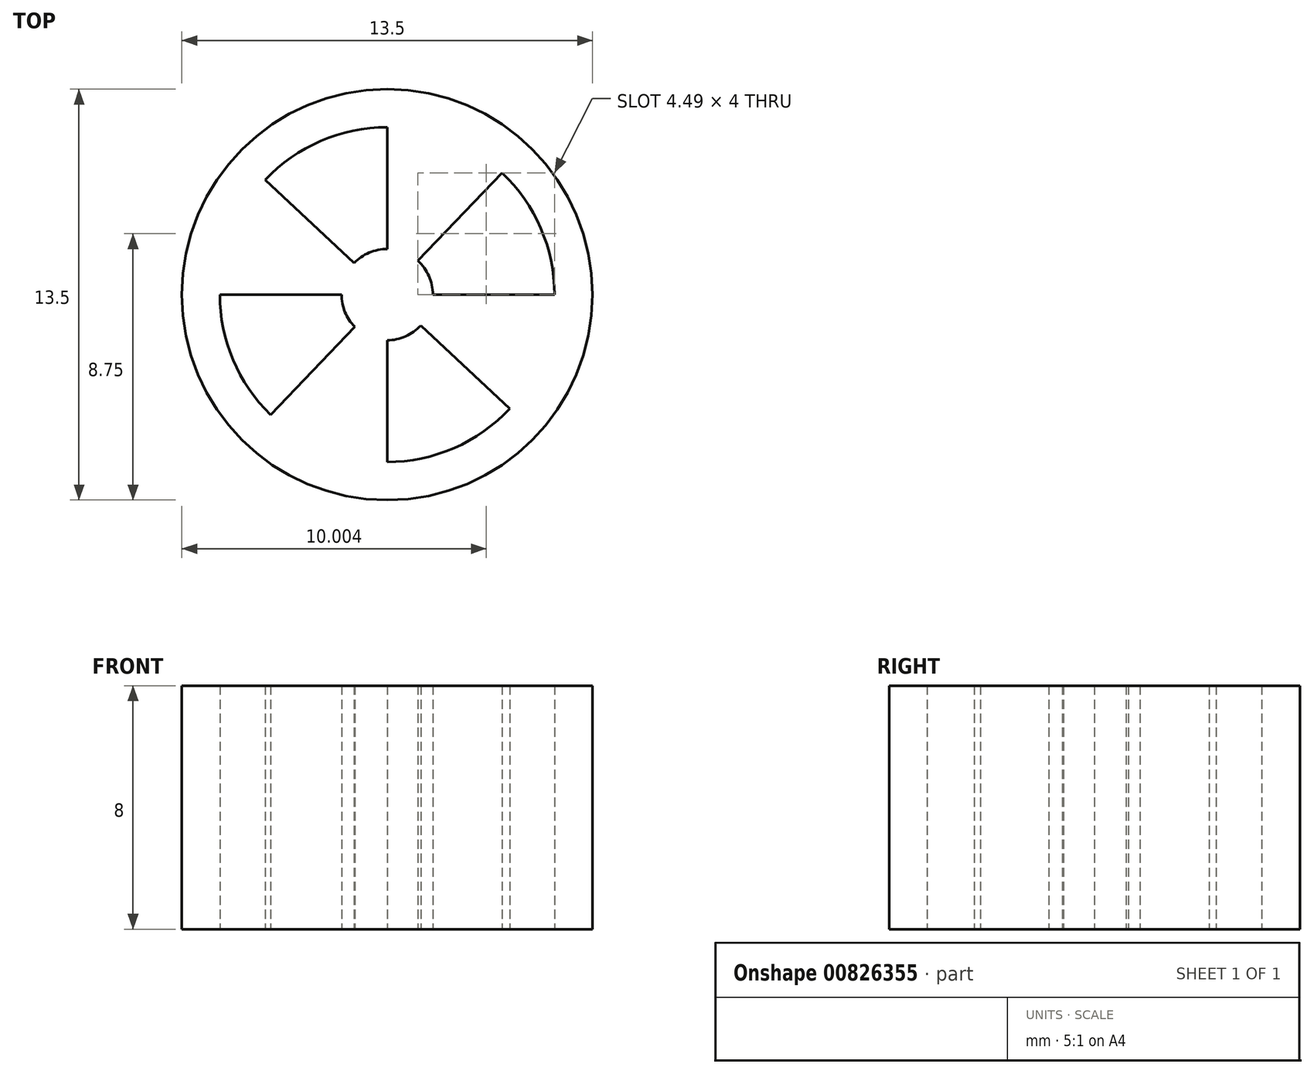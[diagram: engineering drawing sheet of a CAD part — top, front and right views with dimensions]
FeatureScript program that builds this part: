
annotation { "Feature Type Name" : "Feature", "Feature Type Description" : "" }
export const myFeature = defineFeature(function(context is Context, id is Id, definition is map)
    precondition{}
    {
        {
            var Q0;
            Q0=qCreatedBy(makeId("Top.planeOp"),FACE);
            var sketch = newSketch(context, id + "F0", { "sketchPlane" : qUnion([Q0])});
            skCircle(sketch, "E0", {"center": v(0, 0) * mm, "radius": 6.75 * mm});
            skSolve(sketch);
        }
        {
            var Q0;
            Q0=makeQuery(id+"F0.imprint","IMPRINT",FACE,{"disambiguationData":[TD([[makeQuery(id+"F0.imprint","IMPRINT",EDGE,{"derivedFrom":sQuery(id+"F0.wireOp",EDGE,"E0")}),1.0]])]});
            extrude(context, id + "F1", {"entities" : qUnion([Q0]), "depth" : 8 * mm, "offsetDistance" : 25 * mm});
        }
        {
            var Q0;
            Q0=makeQuery(id+"F1.opExtrude","CAP_FACE",FACE,{"disambiguationData":[OSD([sQuery(id+"F0.wireOp",EDGE,"E0")])],"isStart":true});
            var sketch = newSketch(context, id + "F2", { "sketchPlane" : qUnion([Q0])});
            skCircle(sketch, "E1", {"center": v(0, 0) * mm, "radius": 5.5 * mm});
            skCircle(sketch, "E2", {"center": v(0, 0) * mm, "radius": 1.5 * mm});
            skLineSegment(sketch, "E3", {"start": v(0, 0) * mm, "end": v(0, 5.5) * mm});
            skLineSegment(sketch, "E4", {"start": v(0, 0) * mm, "end": v(0, -5.5) * mm});
            skLineSegment(sketch, "E5", {"start": v(0, 0) * mm, "end": v(5.5, 0) * mm});
            skLineSegment(sketch, "E6", {"start": v(0, 0) * mm, "end": v(-5.5, 0) * mm});
            skLineSegment(sketch, "E7", {"start": v(-3.83, 3.95) * mm, "end": v(3.77, -4) * mm});
            skLineSegment(sketch, "E8", {"start": v(4.03, 3.74) * mm, "end": v(-4, -3.77) * mm});
            skSolve(sketch);
        }
        {
            var Q0;
            {var subQ0=sQuery(id+"F2.wireOp",EDGE,"E3");var subQ1=sQuery(id+"F2.wireOp",EDGE,"E1");var subQ2=makeQuery(id+"F2.imprint","INTERSECT",VERTEX,{"derivedFrom":[subQ1,subQ0]});Q0=makeQuery(id+"F2.imprint","IMPRINT",FACE,{"disambiguationData":[TD([[makeQuery(id+"F2.imprint","IMPRINT",EDGE,{"disambiguationData":[TD([[subQ2,1.0]])],"derivedFrom":subQ1}),1.0]])]});}
            var Q1;
            {var subQ0=sQuery(id+"F2.wireOp",EDGE,"E6");var subQ1=sQuery(id+"F2.wireOp",EDGE,"E1");var subQ2=makeQuery(id+"F2.imprint","INTERSECT",VERTEX,{"derivedFrom":[subQ1,subQ0]});Q1=makeQuery(id+"F2.imprint","IMPRINT",FACE,{"disambiguationData":[TD([[makeQuery(id+"F2.imprint","IMPRINT",EDGE,{"disambiguationData":[TD([[subQ2,1.0]])],"derivedFrom":subQ1}),1.0]])]});}
            var Q2;
            {var subQ0=sQuery(id+"F2.wireOp",EDGE,"E4");var subQ1=sQuery(id+"F2.wireOp",EDGE,"E1");var subQ2=makeQuery(id+"F2.imprint","INTERSECT",VERTEX,{"derivedFrom":[subQ1,subQ0]});Q2=makeQuery(id+"F2.imprint","IMPRINT",FACE,{"disambiguationData":[TD([[makeQuery(id+"F2.imprint","IMPRINT",EDGE,{"disambiguationData":[TD([[subQ2,1.0]])],"derivedFrom":subQ1}),1.0]])]});}
            var Q3;
            {var subQ0=sQuery(id+"F2.wireOp",EDGE,"E5");var subQ1=sQuery(id+"F2.wireOp",EDGE,"E1");var subQ2=makeQuery(id+"F2.imprint","INTERSECT",VERTEX,{"derivedFrom":[subQ1,subQ0]});Q3=makeQuery(id+"F2.imprint","IMPRINT",FACE,{"disambiguationData":[TD([[makeQuery(id+"F2.imprint","IMPRINT",EDGE,{"disambiguationData":[TD([[subQ2,1.0]])],"derivedFrom":subQ1}),1.0]])]});}
            extrude(context, id + "F3", {"entities" : qUnion([Q0, Q1, Q2, Q3]), "operationType" : NewBodyOperationType.REMOVE, "endBound" : BoundingType.THROUGH_ALL, "oppositeDirection" : true, "depth" : 25 * mm, "offsetDistance" : 25 * mm});
        }
    });
